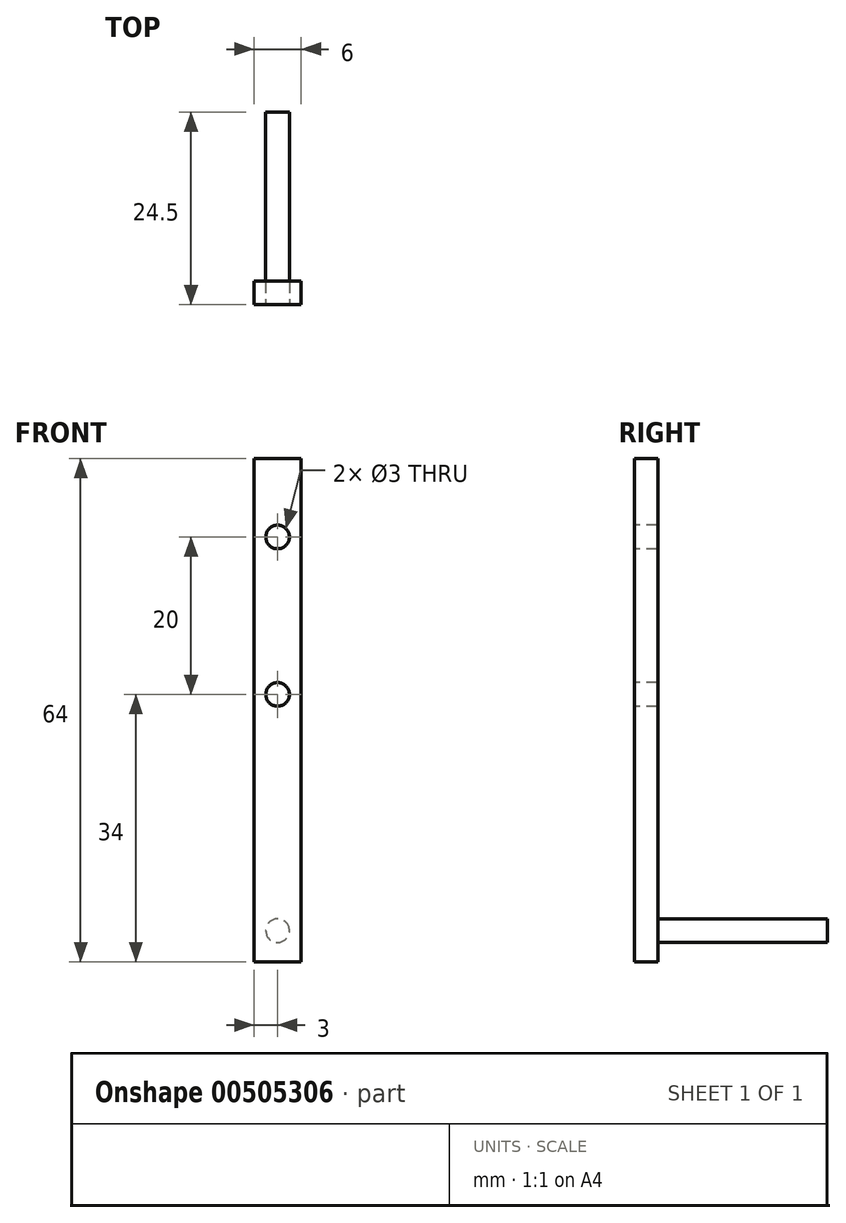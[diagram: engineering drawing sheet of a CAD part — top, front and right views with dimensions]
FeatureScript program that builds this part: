
annotation { "Feature Type Name" : "Feature", "Feature Type Description" : "" }
export const myFeature = defineFeature(function(context is Context, id is Id, definition is map)
    precondition{}
    {
        {
            var Q0;
            Q0=qCreatedBy(makeId("Front.planeOp"),FACE);
            var sketch = newSketch(context, id + "F0", { "sketchPlane" : qUnion([Q0])});
            skLineSegment(sketch, "E0.bottom", {"start": v(3, 32) * mm, "end": v(-3, 32) * mm});
            skLineSegment(sketch, "E0.top", {"start": v(3, -32) * mm, "end": v(-3, -32) * mm});
            skLineSegment(sketch, "E0.left", {"start": v(3, 32) * mm, "end": v(3, -32) * mm});
            skLineSegment(sketch, "E0.right", {"start": v(-3, 32) * mm, "end": v(-3, -32) * mm});
            skPoint(sketch, "E0.middle", {"position": v(0, 0) * mm});
            skSolve(sketch);
        }
        {
            var Q0;
            Q0=makeQuery(id+"F0.imprint","IMPRINT",FACE,{"disambiguationData":[TD([[makeQuery(id+"F0.imprint","IMPRINT",EDGE,{"derivedFrom":sQuery(id+"F0.wireOp",EDGE,"E0.bottom")}),1.0]])]});
            extrude(context, id + "F1", {"entities" : qUnion([Q0]), "depth" : 3 * mm});
        }
        {
            var Q0;
            Q0=makeQuery(id+"F1.opExtrude","CAP_FACE",FACE,{"disambiguationData":[OSD([sQuery(id+"F0.wireOp",EDGE,"E0.bottom"),sQuery(id+"F0.wireOp",EDGE,"E0.top"),sQuery(id+"F0.wireOp",EDGE,"E0.left"),sQuery(id+"F0.wireOp",EDGE,"E0.right")])],"isStart":false});
            var sketch = newSketch(context, id + "F2", { "sketchPlane" : qUnion([Q0])});
            skCircle(sketch, "E1", {"center": v(0, 22) * mm, "radius": 1.5 * mm});
            skCircle(sketch, "E2", {"center": v(0, 2) * mm, "radius": 1.5 * mm});
            skSolve(sketch);
        }
        {
            var Q0;
            Q0=makeQuery(id+"F2.imprint","IMPRINT",FACE,{"disambiguationData":[TD([[makeQuery(id+"F2.imprint","IMPRINT",EDGE,{"derivedFrom":sQuery(id+"F2.wireOp",EDGE,"E2")}),1.0]])]});
            var Q1;
            Q1=makeQuery(id+"F2.imprint","IMPRINT",FACE,{"disambiguationData":[TD([[makeQuery(id+"F2.imprint","IMPRINT",EDGE,{"derivedFrom":sQuery(id+"F2.wireOp",EDGE,"E1")}),1.0]])]});
            extrude(context, id + "F3", {"entities" : qUnion([Q0, Q1]), "operationType" : NewBodyOperationType.REMOVE, "oppositeDirection" : true, "depth" : 5 * mm});
        }
        {
            var Q0;
            Q0=makeQuery(id+"F1.opExtrude","CAP_FACE",FACE,{"disambiguationData":[OSD([sQuery(id+"F0.wireOp",EDGE,"E0.bottom"),sQuery(id+"F0.wireOp",EDGE,"E0.top"),sQuery(id+"F0.wireOp",EDGE,"E0.left"),sQuery(id+"F0.wireOp",EDGE,"E0.right")])],"isStart":false});
            var sketch = newSketch(context, id + "F4", { "sketchPlane" : qUnion([Q0])});
            skCircle(sketch, "E3", {"center": v(0, -28) * mm, "radius": 1.5 * mm});
            skSolve(sketch);
        }
        {
            var Q0;
            Q0=makeQuery(id+"F4.imprint","IMPRINT",FACE,{"disambiguationData":[TD([[makeQuery(id+"F4.imprint","IMPRINT",EDGE,{"derivedFrom":sQuery(id+"F4.wireOp",EDGE,"E3")}),1.0]])]});
            extrude(context, id + "F5", {"entities" : qUnion([Q0]), "operationType" : NewBodyOperationType.ADD, "depth" : -24.5 * mm});
        }
    });
